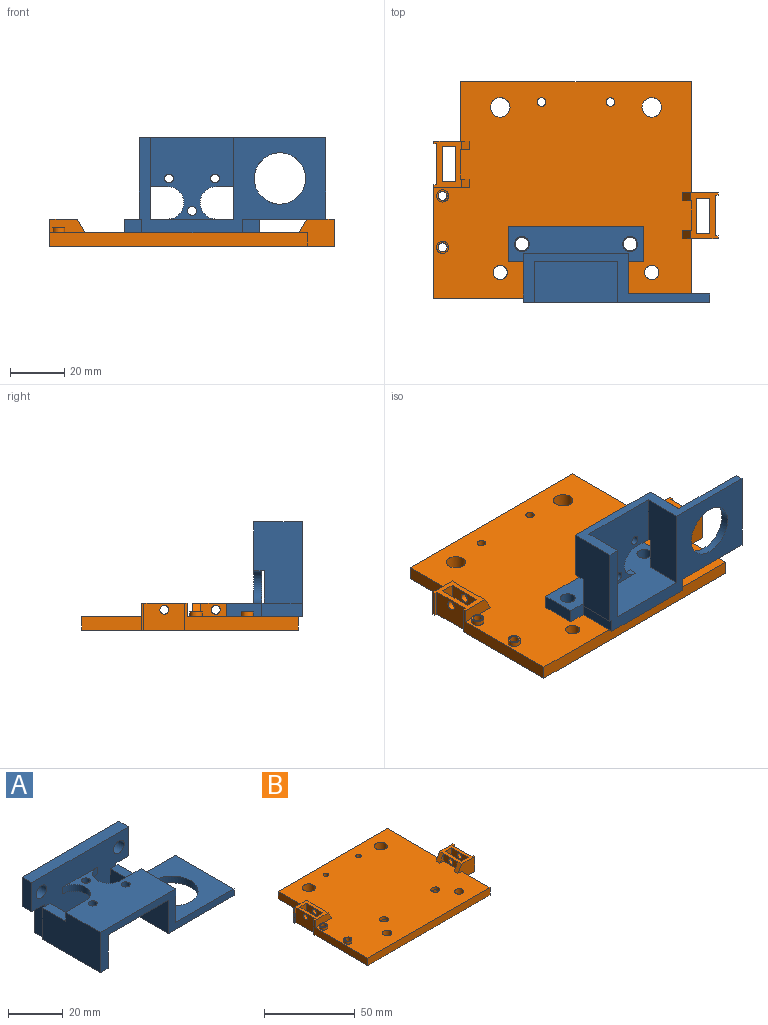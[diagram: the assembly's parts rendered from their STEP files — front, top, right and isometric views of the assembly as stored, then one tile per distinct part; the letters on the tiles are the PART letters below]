
ASSEMBLY  parts=2 mates=1
PART A: 33 faces, bbox 74.5x35x28 mm
  f0: plane 30x15mm, normal (1,0,0), area 402mm2, adj f2,f4,f8,f24,f26,f30
  f1: plane 30x18mm, normal (-1,0,0), area 492mm2, adj f4,f8,f20,f21,f27,f29
  f2: plane 31x14mm, normal (0,1,0), area 104mm2, adj f0,f21,f22,f26,f30,f31
  f3: plane 31x30mm, normal (0,0,-1), area 635.2mm2, adj f5,f6,f8,f12,f14,f15,f16,f24
  f4: plane 39x30mm, normal (0,0,1), area 779.2mm2, adj f0,f1,f8,f12,f14,f15,f16,f24
  f5: plane 30x15mm, normal (1,0,0), area 438mm2, adj f3,f8,f12,f21,f27,f29
  f6: plane 30x15mm, normal (-1,0,0), area 438mm2, adj f3,f8,f12,f21,f24,f26
  f7: plane 6.5x5mm, normal (0,0,-1), area 32.5mm2, adj f9,f10,f12,f22
  f8: plane 69x18mm, normal (0,-1,0), area 327mm2, adj f0,f1,f3,f4,f5,f6,f21,f30
  f9: plane 13x5mm, normal (1,0,0), area 65mm2, adj f7,f10,f12,f17
  f10: plane 50x28mm, normal (0,1,0), area 1157.5mm2, adj f7,f9,f11,f13,f17,f18,f19,f21
  f11: plane 13x5mm, normal (-1,0,0), area 65mm2, adj f10,f12,f13,f17
  f12: plane 50x28mm, normal (0,-1,0), area 1019.5mm2, adj f3,f4,f5,f6,f7,f9,f11,f13
  f13: plane 6.5x5mm, normal (0,0,-1), area 32.5mm2, adj f10,f11,f12,f23
  f14: cylinder r=1.65mm len=3.3mm, axis (0,0,-1), area 31.1mm2, adj f3,f4
  f15: cylinder r=1.65mm len=3.3mm, axis (0,0,-1), area 31.1mm2, adj f3,f4
  f16: cylinder r=1.65mm len=3.3mm, axis (0,0,-1), area 31.1mm2, adj f3,f4
  f17: plane 50x5mm, normal (0,0,1), area 250mm2, adj f9,f10,f11,f12
  f18: cylinder r=2.75mm len=5.5mm, axis (0,-1,0), area 86.4mm2, adj f10,f12
  f19: cylinder r=2.75mm len=5.5mm, axis (0,-1,0), area 86.4mm2, adj f10,f12
  f20: plane 14x1mm, normal (0,1,0), area 14mm2, adj f1,f21,f23,f29
  f21: plane 69x35mm, normal (0,0,-1), area 1041.5mm2, adj f1,f2,f5,f6,f8,f10,f12,f20
  f22: plane 15x5mm, normal (1,0,0), area 75mm2, adj f2,f7,f10,f12,f21
  f23: plane 15x5mm, normal (-1,0,0), area 75mm2, adj f10,f12,f13,f20,f21
  f24: plane 10.5x4mm, normal (0,1,0), area 35.5mm2, adj f0,f3,f4,f6,f25,f26
  f25: cylinder r=6mm len=12mm, axis (0,0,1), area 56.5mm2, adj f3,f4,f12,f24
  f26: plane 12x4mm, normal (0,0,1), area 48mm2, adj f0,f2,f6,f12,f24
  f27: plane 10.5x4mm, normal (0,1,0), area 35.5mm2, adj f1,f3,f4,f5,f28,f29
  f28: cylinder r=6mm len=12mm, axis (0,0,1), area 56.5mm2, adj f3,f4,f12,f27
  f29: plane 12x4mm, normal (0,0,1), area 48mm2, adj f1,f5,f12,f20,f27
  f30: plane 30x30mm, normal (0,0,1), area 616.5mm2, adj f0,f2,f8,f31,f32
  f31: plane 30x3mm, normal (1,0,0), area 90mm2, adj f2,f8,f21,f30
  f32: cylinder r=9.5mm len=19mm, axis (0,0,-1), area 179.1mm2, adj f21,f30
PART B: 87 faces, bbox 105x80x10 mm
  f0: plane 105x80mm, normal (0,0,-1), area 7090.4mm2, adj f3,f4,f6,f7,f8,f9,f10,f11
  f1: cylinder r=1.65mm len=3.3mm, axis (1,0,0), area 20.7mm2, adj f35,f48
  f2: cylinder r=1.65mm len=3.3mm, axis (-1,0,0), area 20.7mm2, adj f13,f44
  f3: plane 41x5mm, normal (1,0,0), area 205mm2, adj f0,f5,f8,f26
  f4: plane 22x5mm, normal (-1,0,0), area 110mm2, adj f0,f5,f8,f16
  f5: plane 95x80mm, normal (0,0,1), area 6961.9mm2, adj f3,f4,f6,f7,f8,f9,f10,f11
  f6: plane 95x5mm, normal (0,-1,0), area 475mm2, adj f0,f5,f7,f21
  f7: plane 22x5mm, normal (1,0,0), area 110mm2, adj f0,f5,f6,f32
  f8: plane 85x5mm, normal (0,1,0), area 425mm2, adj f0,f3,f4,f5
  f9: cylinder r=2.62mm len=5.25mm, axis (0,0,-1), area 82.5mm2, adj f0,f5
  f10: cylinder r=2.62mm len=5.25mm, axis (0,0,-1), area 82.5mm2, adj f0,f5
  f11: cylinder r=3.62mm len=7.23mm, axis (0,0,-1), area 113.6mm2, adj f0,f5
  f12: cylinder r=3.62mm len=7.23mm, axis (0,0,-1), area 113.6mm2, adj f0,f5
  f13: plane 11x5mm, normal (1,0,0), area 46.4mm2, adj f2,f5,f14,f24,f25
  f14: plane 5x3mm, normal (0,-1,0), area 7.8mm2, adj f5,f13,f15,f25
  f15: plane 5x3mm, normal (0.87,0,0.5), area 17.3mm2, adj f5,f14,f16,f25
  f16: plane 13x10mm, normal (0,1,0), area 107.8mm2, adj f0,f4,f5,f15,f17,f25
  f17: plane 10x1mm, normal (-1,0,0), area 10mm2, adj f0,f16,f18,f25
  f18: plane 10x1mm, normal (0,-1,0), area 10mm2, adj f0,f17,f19,f25
  f19: plane 15x10mm, normal (-1,0,0), area 141.4mm2, adj f0,f18,f20,f25,f40
  f20: plane 10x1mm, normal (0,1,0), area 10mm2, adj f0,f19,f21,f25
  f21: plane 42x10mm, normal (-1,0,0), area 215mm2, adj f0,f5,f6,f20,f22,f25
  f22: plane 13x5mm, normal (0,-1,0), area 57.8mm2, adj f5,f21,f23,f25
  f23: plane 5x3mm, normal (0.87,0,0.5), area 17.3mm2, adj f5,f22,f24,f25
  f24: plane 5x3mm, normal (0,1,0), area 7.8mm2, adj f5,f13,f23,f25
  f25: plane 17x10.11mm, normal (0,0,1), area 90.7mm2, adj f13,f14,f15,f16,f17,f18,f19,f20
  f26: plane 13x10mm, normal (0,1,0), area 107.8mm2, adj f0,f3,f5,f27,f37,f38
  f27: plane 5x3mm, normal (-0.87,0,0.5), area 17.3mm2, adj f5,f26,f28,f38
  f28: plane 5x3mm, normal (0,-1,0), area 7.8mm2, adj f5,f27,f29,f38
  f29: plane 11x5mm, normal (-1,0,0), area 46.4mm2, adj f5,f28,f30,f38,f39
  f30: plane 5x3mm, normal (0,1,0), area 7.8mm2, adj f5,f29,f31,f38
  f31: plane 5x3mm, normal (-0.87,0,0.5), area 17.3mm2, adj f5,f30,f32,f38
  f32: plane 13x10mm, normal (0,-1,0), area 107.8mm2, adj f0,f5,f7,f31,f33,f38
  f33: plane 10x1mm, normal (1,0,0), area 10mm2, adj f0,f32,f34,f38
  f34: plane 10x1mm, normal (0,1,0), area 10mm2, adj f0,f33,f35,f38
  f35: plane 15x10mm, normal (1,0,0), area 141.4mm2, adj f0,f1,f34,f36,f38
  f36: plane 10x1mm, normal (0,-1,0), area 10mm2, adj f0,f35,f37,f38
  f37: plane 10x1mm, normal (1,0,0), area 10mm2, adj f0,f26,f36,f38
  f38: plane 17x10.11mm, normal (0,0,1), area 90.7mm2, adj f26,f27,f28,f29,f30,f31,f32,f33
  f39: cylinder r=1.65mm len=3.3mm, axis (1,0,0), area 20.7mm2, adj f29,f47
  f40: cylinder r=1.65mm len=3.3mm, axis (-1,0,0), area 20.7mm2, adj f19,f43
  f41: plane 10x5mm, normal (0,1,0), area 50mm2, adj f0,f25,f43,f44
  f42: plane 10x5mm, normal (0,-1,0), area 50mm2, adj f0,f25,f43,f44
  f43: plane 13x10mm, normal (1,0,0), area 121.4mm2, adj f0,f25,f40,f41,f42
  f44: plane 13x10mm, normal (-1,0,0), area 121.4mm2, adj f0,f2,f25,f41,f42
  f45: plane 10x5mm, normal (0,1,0), area 50mm2, adj f0,f38,f47,f48
  f46: plane 10x5mm, normal (0,-1,0), area 50mm2, adj f0,f38,f47,f48
  f47: plane 13x10mm, normal (1,0,0), area 121.4mm2, adj f0,f38,f39,f45,f46
  f48: plane 13x10mm, normal (-1,0,0), area 121.4mm2, adj f0,f1,f38,f45,f46
  f49: cylinder r=2.25mm len=4.5mm, axis (0,0,-1), area 24mm2, adj f5,f50
  f50: plane 4.5x4.5mm, normal (0,0,1), area 7.4mm2, adj f49,f67
  f51: cylinder r=2.25mm len=4.5mm, axis (0,0,-1), area 24mm2, adj f5,f52
  f52: plane 4.5x4.5mm, normal (0,0,1), area 7.4mm2, adj f51,f68
  f53: plane 2.7x2.5mm, normal (-0.5,0.87,0), area 7.8mm2, adj f0,f54,f58,f59
  f54: plane 2.7x2.5mm, normal (0.5,0.87,0), area 7.8mm2, adj f0,f53,f55,f59
  f55: plane 3.12x2.5mm, normal (1,0,0), area 7.8mm2, adj f0,f54,f56,f59
  f56: plane 2.7x2.5mm, normal (0.5,-0.87,0), area 7.8mm2, adj f0,f55,f57,f59
  f57: plane 2.7x2.5mm, normal (-0.5,-0.87,0), area 7.8mm2, adj f0,f56,f58,f59
  f58: plane 3.12x2.5mm, normal (-1,0,0), area 7.8mm2, adj f0,f53,f57,f59
  f59: plane 6.24x5.4mm, normal (0,0,-1), area 16.7mm2, adj f53,f54,f55,f56,f57,f58,f67
  f60: plane 2.7x2.5mm, normal (0.5,0.87,0), area 7.8mm2, adj f0,f61,f65,f66
  f61: plane 3.12x2.5mm, normal (1,0,0), area 7.8mm2, adj f0,f60,f62,f66
  f62: plane 2.7x2.5mm, normal (0.5,-0.87,0), area 7.8mm2, adj f0,f61,f63,f66
  f63: plane 2.7x2.5mm, normal (-0.5,-0.87,0), area 7.8mm2, adj f0,f62,f64,f66
  f64: plane 3.12x2.5mm, normal (-1,0,0), area 7.8mm2, adj f0,f63,f65,f66
  f65: plane 2.7x2.5mm, normal (-0.5,0.87,0), area 7.8mm2, adj f0,f60,f64,f66
  f66: plane 6.24x5.4mm, normal (0,0,-1), area 16.7mm2, adj f60,f61,f62,f63,f64,f65,f68
  f67: cylinder r=1.65mm len=4.2mm, axis (0,0,-1), area 43.5mm2, adj f50,f59
  f68: cylinder r=1.65mm len=4.2mm, axis (0,0,-1), area 43.5mm2, adj f52,f66
  f69: plane 3.95x3mm, normal (0.5,-0.87,0), area 13.7mm2, adj f0,f70,f74,f75
  f70: plane 4.56x3mm, normal (1,0,0), area 13.7mm2, adj f0,f69,f71,f75
  f71: plane 3.95x3mm, normal (0.5,0.87,0), area 13.7mm2, adj f0,f70,f72,f75
  f72: plane 3.95x3mm, normal (-0.5,0.87,0), area 13.7mm2, adj f0,f71,f73,f75
  f73: plane 4.56x3mm, normal (-1,0,0), area 13.7mm2, adj f0,f72,f74,f75
  f74: plane 3.95x3mm, normal (-0.5,-0.87,0), area 13.7mm2, adj f0,f69,f73,f75
  f75: plane 9.12x7.9mm, normal (0,0,-1), area 34.4mm2, adj f69,f70,f71,f72,f73,f74,f84
  f76: plane 4.56x3mm, normal (-1,0,0), area 13.7mm2, adj f0,f77,f81,f82
  f77: plane 3.95x3mm, normal (-0.5,-0.87,0), area 13.7mm2, adj f0,f76,f78,f82
  f78: plane 3.95x3mm, normal (0.5,-0.87,0), area 13.7mm2, adj f0,f77,f79,f82
  f79: plane 4.56x3mm, normal (1,0,0), area 13.7mm2, adj f0,f78,f80,f82
  f80: plane 3.95x3mm, normal (0.5,0.87,0), area 13.7mm2, adj f0,f79,f81,f82
  f81: plane 3.95x3mm, normal (-0.5,0.87,0), area 13.7mm2, adj f0,f76,f80,f82
  f82: plane 9.12x7.9mm, normal (0,0,-1), area 34.4mm2, adj f76,f77,f78,f79,f80,f81,f83
  f83: cylinder r=2.5mm len=5mm, axis (0,0,-1), area 31.4mm2, adj f5,f82
  f84: cylinder r=2.5mm len=5mm, axis (0,0,-1), area 31.4mm2, adj f5,f75
  f85: cylinder r=1.57mm len=5mm, axis (0,0,1), area 49.5mm2, adj f0,f5
  f86: cylinder r=1.57mm len=5mm, axis (0,0,1), area 49.5mm2, adj f0,f5
PLACE A rot(axis=(-1,0,0),90deg) t=(7.66,-41.01,26.1)mm
PLACE B t=(7.66,-14.51,7.1)mm
MATE fastened A.f18 <-> B.f83  axis (0,0,1) through (-12.34,-34.51,12.1)mm
